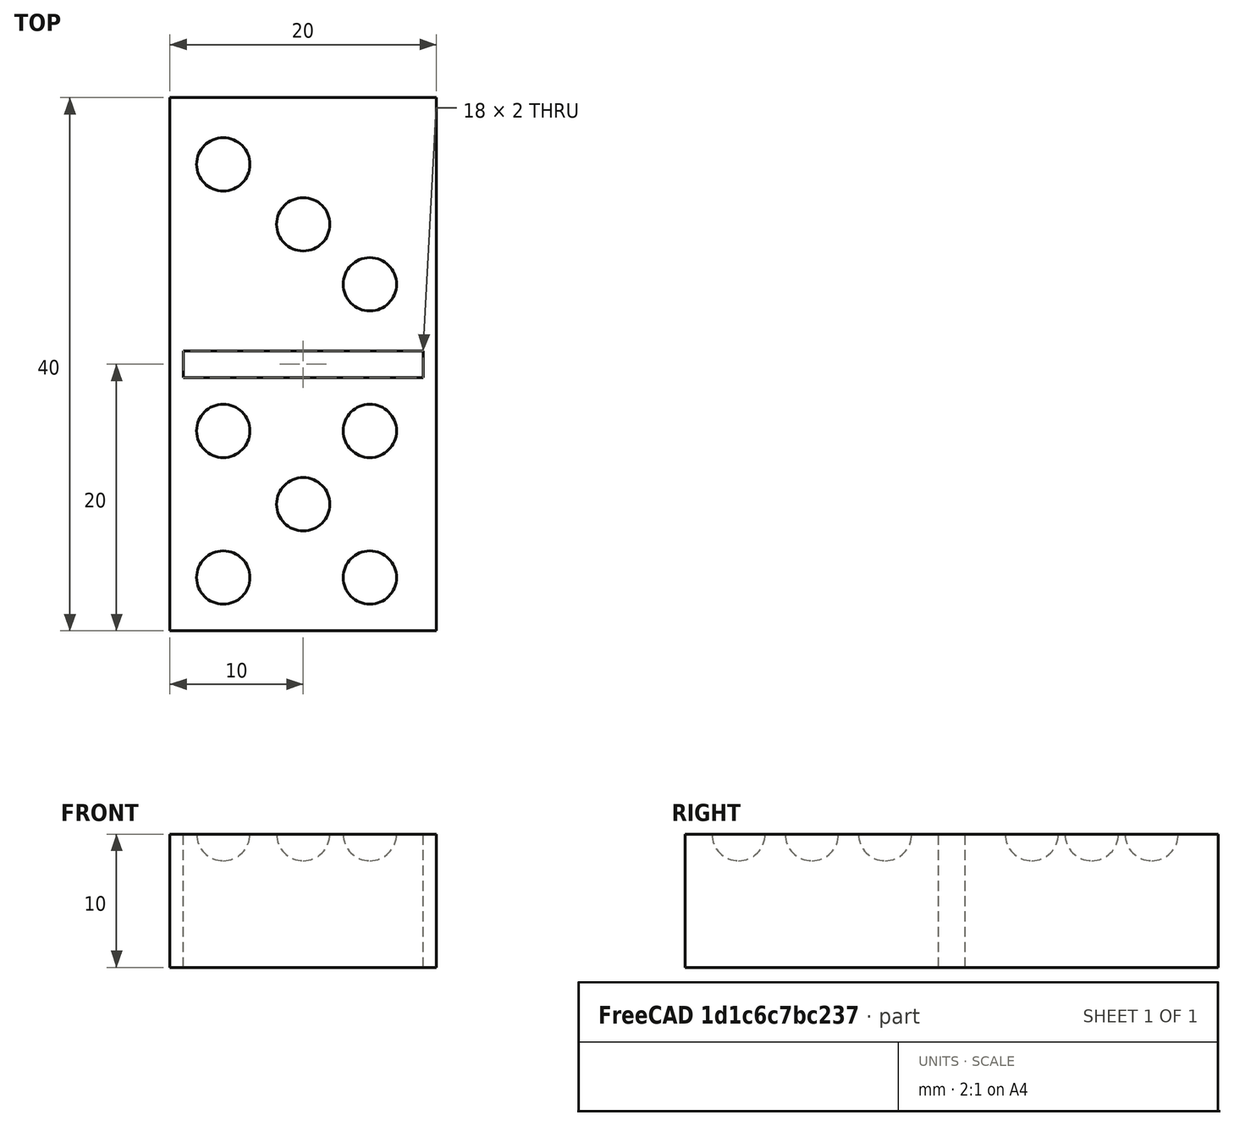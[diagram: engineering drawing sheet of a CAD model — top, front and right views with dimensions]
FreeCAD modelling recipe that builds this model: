
FCSTD DOCUMENT  (FreeCAD 0.21R33694 (Git))
Label: OJT1_T13R03_domino
License: All rights reserved
LicenseURL: http://en.wikipedia.org/wiki/All_rights_reserved
objects: Part::Cut×9, Part::Sphere×8, Part::Box×2
note: 19 computed .brp shape members not serialized (recipe doc carries the construction recipe); baked Part::Feature solids carry a one-line shape summary decoded from their .brp

FEATURE [Part::Box] Box  label="Cube"
  AttacherType = Attacher::AttachEngine3D
  Height = 10
  Length = 20
  Width = 40
FEATURE [Part::Box] Box001  label="Cube001"
  AttacherType = Attacher::AttachEngine3D
  Height = 10
  Length = 18
  Placement = pos=(1,19,0) rot=(0,0,1;0rad)
  Width = 2
FEATURE [Part::Cut] Cut
  Base = -> Box
  Refine = true
  Tool = -> Box001
FEATURE [Part::Sphere] Sphere
  Angle1 = -90
  Angle2 = 90
  Angle3 = 360
  AttacherType = Attacher::AttachEngine3D
  Placement = pos=(10,9.5,10) rot=(0,0,1;0rad)
  Radius = 2
FEATURE [Part::Sphere] Sphere001
  Angle1 = -90
  Angle2 = 90
  Angle3 = 360
  AttacherType = Attacher::AttachEngine3D
  Placement = pos=(4,4,10) rot=(0,0,1;0rad)
  Radius = 2
FEATURE [Part::Sphere] Sphere002
  Angle1 = -90
  Angle2 = 90
  Angle3 = 360
  AttacherType = Attacher::AttachEngine3D
  Placement = pos=(15,4,10) rot=(0,0,1;0rad)
  Radius = 2
FEATURE [Part::Sphere] Sphere003
  Angle1 = -90
  Angle2 = 90
  Angle3 = 360
  AttacherType = Attacher::AttachEngine3D
  Placement = pos=(4,35,10) rot=(0,0,1;0rad)
  Radius = 2
FEATURE [Part::Sphere] Sphere004
  Angle1 = -90
  Angle2 = 90
  Angle3 = 360
  AttacherType = Attacher::AttachEngine3D
  Placement = pos=(15,15,10) rot=(0,0,1;0rad)
  Radius = 2
FEATURE [Part::Sphere] Sphere005
  Angle1 = -90
  Angle2 = 90
  Angle3 = 360
  AttacherType = Attacher::AttachEngine3D
  Placement = pos=(10,30.5,10) rot=(0,0,1;0rad)
  Radius = 2
FEATURE [Part::Sphere] Sphere006
  Angle1 = -90
  Angle2 = 90
  Angle3 = 360
  AttacherType = Attacher::AttachEngine3D
  Placement = pos=(4,15,10) rot=(0,0,1;0rad)
  Radius = 2
FEATURE [Part::Sphere] Sphere007
  Angle1 = -90
  Angle2 = 90
  Angle3 = 360
  AttacherType = Attacher::AttachEngine3D
  Placement = pos=(15,26,10) rot=(0,0,1;0rad)
  Radius = 2
FEATURE [Part::Cut] Cut001
  Base = -> Cut
  Refine = true
  Tool = -> Sphere
FEATURE [Part::Cut] Cut002
  Base = -> Cut001
  Refine = true
  Tool = -> Sphere007
FEATURE [Part::Cut] Cut003
  Base = -> Cut002
  Refine = true
  Tool = -> Sphere006
FEATURE [Part::Cut] Cut004
  Base = -> Cut003
  Refine = true
  Tool = -> Sphere005
FEATURE [Part::Cut] Cut005
  Base = -> Cut004
  Refine = true
  Tool = -> Sphere004
FEATURE [Part::Cut] Cut006
  Base = -> Cut005
  Refine = true
  Tool = -> Sphere003
FEATURE [Part::Cut] Cut007
  Base = -> Cut006
  Refine = true
  Tool = -> Sphere002
FEATURE [Part::Cut] Cut008
  Base = -> Cut007
  Refine = true
  Tool = -> Sphere001
